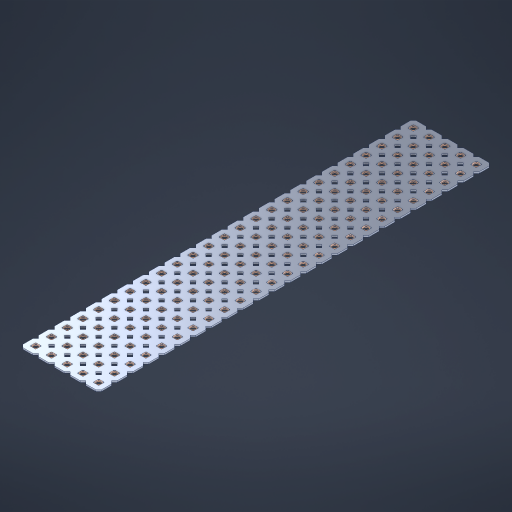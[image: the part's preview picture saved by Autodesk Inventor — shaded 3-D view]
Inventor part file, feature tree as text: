
AUTODESK INVENTOR PART (.ipt)
format: ipt  version: 2023 (Build 270158000, 158)  size: 1,707,520 bytes
history: native  units: in
note: dims shown in document units (in); Inventor stores cm internally (conversion verified against a paired STEP export)
features: other x126, extrude x124, sketch x2, pattern_linear x1
ambient origin geometry x8: Origin, YZ Plane, XZ Plane, XY Plane, X Axis, Y Axis, Z Axis, Center Point
bodies: Solid1 (feature_tree), Body (feature_tree)
feature tree (253):
  pattern_linear  "Rectangular Pattern1"  Spacing1=0.09in  [1 undecoded]
  sketch  "Sketch1"  dims[d1=0.5in]
  sketch  "Sketch2"  dims[d2=0.182in d3=0.09in d4=0.09in d5=0.09in d6=0.09in d7=0.09in d8=0.09in d9=0.09in d10=0.09in d11=0.02in d13=0.0in d14=0.172in d15=0.0625in d16=0.0in d19=0.5in d22=0.5in]
  other  "Srf1"
  other  "Srf126"
  other  "Srf127"
  other  "Srf128"
  other  "Srf129"
  other  "Srf130"
  other  "Srf131"
  other  "Srf250"
  other  "Srf251"
  other  "Srf252"
  other  "Srf253"
  other  "Srf254"
  other  "Srf255"
  other  "Srf256"
  other  "Srf257"
  other  "Srf258"
  other  "Srf259"
  other  "Srf260"
  other  "Srf261"
  other  "Srf262"
  other  "Srf263"
  other  "Srf264"
  other  "Srf265"
  other  "Srf266"
  other  "Srf267"
  other  "Srf268"
  other  "Srf269"
  other  "Srf270"
  other  "Srf271"
  other  "Srf272"
  other  "Srf273"
  other  "Srf274"
  other  "Srf275"
  other  "Srf276"
  other  "Srf277"
  other  "Srf278"
  other  "Srf279"
  other  "Srf280"
  other  "Srf281"
  other  "Srf282"
  other  "Srf283"
  other  "Srf284"
  other  "Srf285"
  other  "Srf286"
  other  "Srf287"
  other  "Srf288"
  other  "Srf289"
  other  "Srf290"
  other  "Srf291"
  other  "Srf292"
  other  "Srf293"
  other  "Srf294"
  other  "Srf295"
  other  "Srf296"
  other  "Srf297"
  other  "Srf298"
  other  "Srf299"
  other  "Srf300"
  other  "Srf301"
  other  "Srf302"
  other  "Srf303"
  other  "Srf304"
  other  "Srf305"
  other  "Srf306"
  other  "Srf307"
  other  "Srf308"
  other  "Srf309"
  other  "Srf310"
  other  "Srf311"
  other  "Srf312"
  other  "Srf313"
  other  "Srf314"
  other  "Srf315"
  other  "Srf316"
  other  "Srf317"
  other  "Srf318"
  other  "Srf319"
  other  "Srf320"
  other  "Srf321"
  other  "Srf322"
  other  "Srf323"
  other  "Srf324"
  other  "Srf325"
  other  "Srf326"
  other  "Srf327"
  other  "Srf328"
  other  "Srf329"
  other  "Srf330"
  other  "Srf331"
  other  "Srf332"
  other  "Srf333"
  other  "Srf334"
  other  "Srf335"
  other  "Srf336"
  other  "Srf337"
  other  "Srf338"
  other  "Srf339"
  other  "Srf340"
  other  "Srf341"
  other  "Srf342"
  other  "Srf343"
  other  "Srf344"
  other  "Srf345"
  other  "Srf346"
  other  "Srf347"
  other  "Srf348"
  other  "Srf349"
  other  "Srf350"
  other  "Srf351"
  other  "Srf352"
  other  "Srf353"
  other  "Srf354"
  other  "Srf355"
  other  "Srf356"
  other  "Srf357"
  other  "Srf358"
  other  "Srf359"
  other  "Srf360"
  other  "Srf361"
  other  "Srf362"
  other  "Srf363"
  other  "Srf364"
  other  "Srf365"
  other  "Srf366"
  other  "Srf367"
  other  "Circle"
  extrude  "ExtrusionSrf126"  Depth=0.09in
  extrude  "ExtrusionSrf127"  Depth=0.09in
  extrude  "ExtrusionSrf128"  Depth=0.09in
  extrude  "ExtrusionSrf129"  Depth=0.09in
  extrude  "ExtrusionSrf130"  Depth=0.09in
  extrude  "ExtrusionSrf131"  Depth=0.09in
  extrude  "ExtrusionSrf250"  Depth=0.09in
  extrude  "ExtrusionSrf251"  Depth=0.02in
  extrude  "ExtrusionSrf252"  TaperAngle=0.0deg  [1 undecoded]
  extrude  "ExtrusionSrf253"  Depth=0.5in
  extrude  "ExtrusionSrf254"  Depth=0.5in TaperAngle=0.0deg
  extrude  "ExtrusionSrf255"  Depth=0.5in
  extrude  "ExtrusionSrf256"  Depth=0.5in
  extrude  "ExtrusionSrf257"  [1 undecoded]
  extrude  "ExtrusionSrf258"  [1 undecoded]
  extrude  "ExtrusionSrf259"  [1 undecoded]
  extrude  "ExtrusionSrf260"  [1 undecoded]
  extrude  "ExtrusionSrf261"  [1 undecoded]
  extrude  "ExtrusionSrf262"  [1 undecoded]
  extrude  "ExtrusionSrf263"  [1 undecoded]
  extrude  "ExtrusionSrf264"  [1 undecoded]
  extrude  "ExtrusionSrf265"  [1 undecoded]
  extrude  "ExtrusionSrf266"  [1 undecoded]
  extrude  "ExtrusionSrf267"  [1 undecoded]
  extrude  "ExtrusionSrf268"  [1 undecoded]
  extrude  "ExtrusionSrf269"  [1 undecoded]
  extrude  "ExtrusionSrf270"  [1 undecoded]
  extrude  "ExtrusionSrf271"  [1 undecoded]
  extrude  "ExtrusionSrf272"  [1 undecoded]
  extrude  "ExtrusionSrf273"  [1 undecoded]
  extrude  "ExtrusionSrf274"  [1 undecoded]
  extrude  "ExtrusionSrf275"  [1 undecoded]
  extrude  "ExtrusionSrf276"  [1 undecoded]
  extrude  "ExtrusionSrf277"  [1 undecoded]
  extrude  "ExtrusionSrf278"  [1 undecoded]
  extrude  "ExtrusionSrf279"  [1 undecoded]
  extrude  "ExtrusionSrf280"  [1 undecoded]
  extrude  "ExtrusionSrf281"  [1 undecoded]
  extrude  "ExtrusionSrf282"  [1 undecoded]
  extrude  "ExtrusionSrf283"  [1 undecoded]
  extrude  "ExtrusionSrf284"  [1 undecoded]
  extrude  "ExtrusionSrf285"  [1 undecoded]
  extrude  "ExtrusionSrf286"  [1 undecoded]
  extrude  "ExtrusionSrf287"  [1 undecoded]
  extrude  "ExtrusionSrf288"  [1 undecoded]
  extrude  "ExtrusionSrf289"  [1 undecoded]
  extrude  "ExtrusionSrf290"  [1 undecoded]
  extrude  "ExtrusionSrf291"  [1 undecoded]
  extrude  "ExtrusionSrf292"  [1 undecoded]
  extrude  "ExtrusionSrf293"  [1 undecoded]
  extrude  "ExtrusionSrf294"  [1 undecoded]
  extrude  "ExtrusionSrf295"  [1 undecoded]
  extrude  "ExtrusionSrf296"  [1 undecoded]
  extrude  "ExtrusionSrf297"  [1 undecoded]
  extrude  "ExtrusionSrf298"  [1 undecoded]
  extrude  "ExtrusionSrf299"  [1 undecoded]
  extrude  "ExtrusionSrf300"  [1 undecoded]
  extrude  "ExtrusionSrf301"  [1 undecoded]
  extrude  "ExtrusionSrf302"  [1 undecoded]
  extrude  "ExtrusionSrf303"  [1 undecoded]
  extrude  "ExtrusionSrf304"  [1 undecoded]
  extrude  "ExtrusionSrf305"  [1 undecoded]
  extrude  "ExtrusionSrf306"  [1 undecoded]
  extrude  "ExtrusionSrf307"  [1 undecoded]
  extrude  "ExtrusionSrf308"  [1 undecoded]
  extrude  "ExtrusionSrf309"  [1 undecoded]
  extrude  "ExtrusionSrf310"  [1 undecoded]
  extrude  "ExtrusionSrf311"  [1 undecoded]
  extrude  "ExtrusionSrf312"  [1 undecoded]
  extrude  "ExtrusionSrf313"  [1 undecoded]
  extrude  "ExtrusionSrf314"  [1 undecoded]
  extrude  "ExtrusionSrf315"  [1 undecoded]
  extrude  "ExtrusionSrf316"  [1 undecoded]
  extrude  "ExtrusionSrf317"  [1 undecoded]
  extrude  "ExtrusionSrf318"  [1 undecoded]
  extrude  "ExtrusionSrf319"  [1 undecoded]
  extrude  "ExtrusionSrf320"  [1 undecoded]
  extrude  "ExtrusionSrf321"  [1 undecoded]
  extrude  "ExtrusionSrf322"  [1 undecoded]
  extrude  "ExtrusionSrf323"  [1 undecoded]
  extrude  "ExtrusionSrf324"  [1 undecoded]
  extrude  "ExtrusionSrf325"  [1 undecoded]
  extrude  "ExtrusionSrf326"  [1 undecoded]
  extrude  "ExtrusionSrf327"  [1 undecoded]
  extrude  "ExtrusionSrf328"  [1 undecoded]
  extrude  "ExtrusionSrf329"  [1 undecoded]
  extrude  "ExtrusionSrf330"  [1 undecoded]
  extrude  "ExtrusionSrf331"  [1 undecoded]
  extrude  "ExtrusionSrf332"  [1 undecoded]
  extrude  "ExtrusionSrf333"  [1 undecoded]
  extrude  "ExtrusionSrf334"  [1 undecoded]
  extrude  "ExtrusionSrf335"  [1 undecoded]
  extrude  "ExtrusionSrf336"  [1 undecoded]
  extrude  "ExtrusionSrf337"  [1 undecoded]
  extrude  "ExtrusionSrf338"  [1 undecoded]
  extrude  "ExtrusionSrf339"  [1 undecoded]
  extrude  "ExtrusionSrf340"  [1 undecoded]
  extrude  "ExtrusionSrf341"  [1 undecoded]
  extrude  "ExtrusionSrf342"  [1 undecoded]
  extrude  "ExtrusionSrf343"  [1 undecoded]
  extrude  "ExtrusionSrf344"  [1 undecoded]
  extrude  "ExtrusionSrf345"  [1 undecoded]
  extrude  "ExtrusionSrf346"  [1 undecoded]
  extrude  "ExtrusionSrf347"  [1 undecoded]
  extrude  "ExtrusionSrf348"  [1 undecoded]
  extrude  "ExtrusionSrf349"  [1 undecoded]
  extrude  "ExtrusionSrf350"  [1 undecoded]
  extrude  "ExtrusionSrf351"  [1 undecoded]
  extrude  "ExtrusionSrf352"  [1 undecoded]
  extrude  "ExtrusionSrf353"  [1 undecoded]
  extrude  "ExtrusionSrf354"  [1 undecoded]
  extrude  "ExtrusionSrf355"  [1 undecoded]
  extrude  "ExtrusionSrf356"  [1 undecoded]
  extrude  "ExtrusionSrf357"  [1 undecoded]
  extrude  "ExtrusionSrf358"  [1 undecoded]
  extrude  "ExtrusionSrf359"  [1 undecoded]
  extrude  "ExtrusionSrf360"  [1 undecoded]
  extrude  "ExtrusionSrf361"  [1 undecoded]
  extrude  "ExtrusionSrf362"  [1 undecoded]
  extrude  "ExtrusionSrf363"  [1 undecoded]
  extrude  "ExtrusionSrf364"  [1 undecoded]
  extrude  "ExtrusionSrf365"  [1 undecoded]
  extrude  "ExtrusionSrf366"  [1 undecoded]
  extrude  "ExtrusionSrf367"  [1 undecoded]
note: 113 required parameter values undecoded (feature->parameter linkage not recoverable at this tier; creation-order binding heuristic only, values carry confidence <= 0.55)
